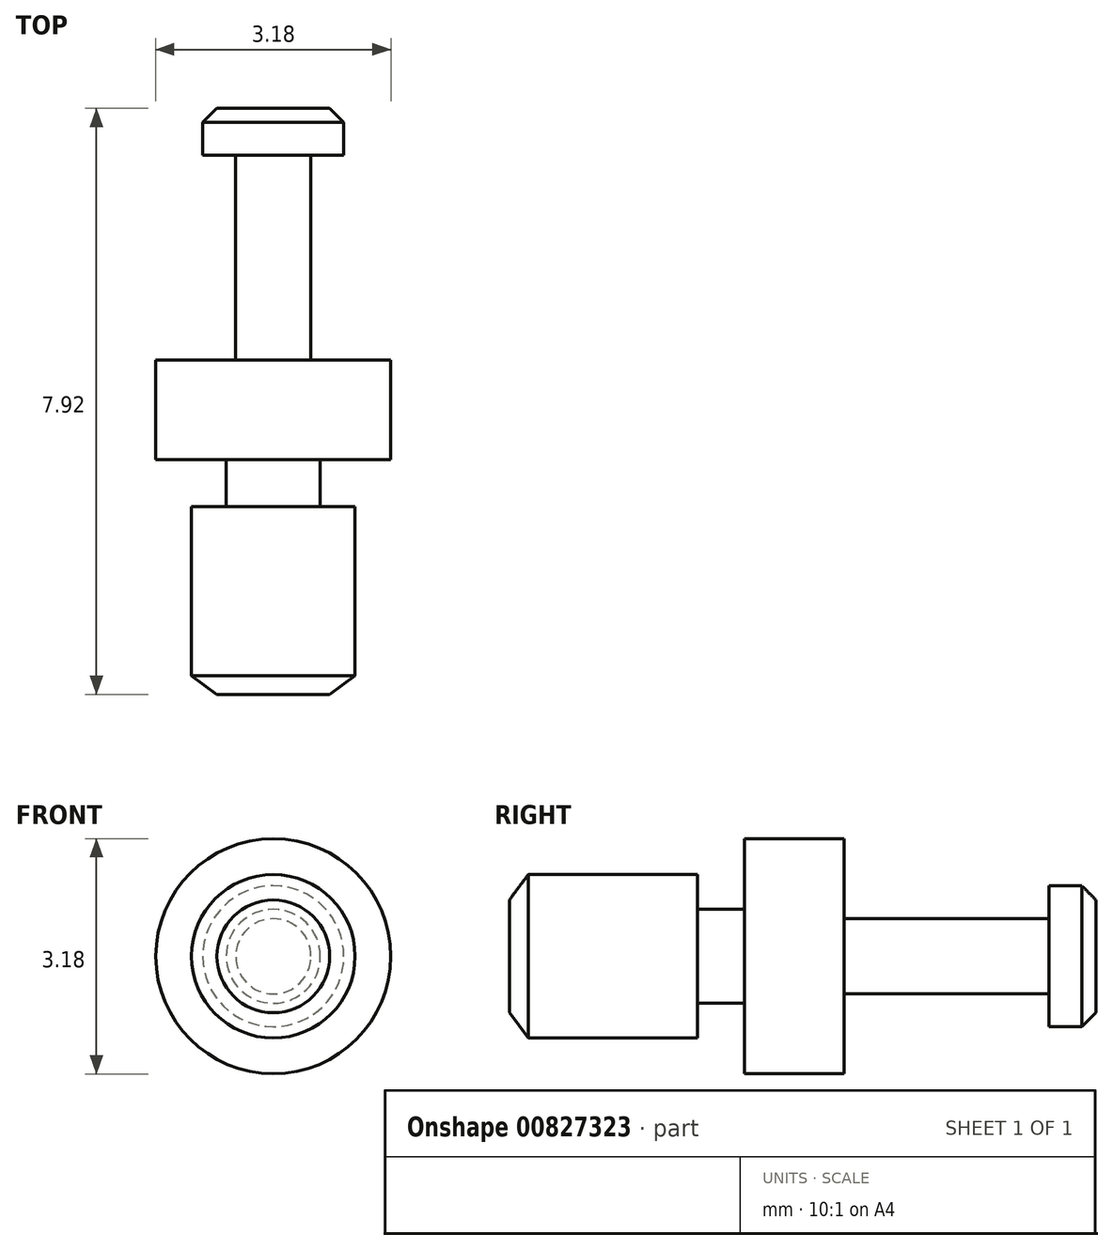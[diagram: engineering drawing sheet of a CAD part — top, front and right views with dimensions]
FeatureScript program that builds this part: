
annotation { "Feature Type Name" : "Feature", "Feature Type Description" : "" }
export const myFeature = defineFeature(function(context is Context, id is Id, definition is map)
    precondition{}
    {
        {
            var Q0;
            Q0=qCreatedBy(makeId("Top.planeOp"),FACE);
            var sketch = newSketch(context, id + "F0", { "sketchPlane" : qUnion([Q0])});
            skLineSegment(sketch, "E0", {"start": v(0, 7.92) * mm, "end": v(0, 0) * mm});
            skLineSegment(sketch, "E1", {"start": v(0, 7.92) * mm, "end": v(-0.76, 7.92) * mm});
            skLineSegment(sketch, "E2", {"start": v(-0.95, 7.29) * mm, "end": v(-0.5, 7.29) * mm});
            skLineSegment(sketch, "E3", {"start": v(-0.5, 7.29) * mm, "end": v(-0.5, 4.52) * mm});
            skLineSegment(sketch, "E4", {"start": v(-0.5, 4.52) * mm, "end": v(-1.59, 4.52) * mm});
            skLineSegment(sketch, "E5", {"start": v(-1.59, 4.52) * mm, "end": v(-1.59, 3.17) * mm});
            skLineSegment(sketch, "E6", {"start": v(-1.59, 3.17) * mm, "end": v(-0.63, 3.17) * mm});
            skLineSegment(sketch, "E7", {"start": v(-0.63, 3.17) * mm, "end": v(-0.63, 2.54) * mm});
            skLineSegment(sketch, "E8", {"start": v(-0.63, 2.54) * mm, "end": v(-1.1, 2.54) * mm});
            skLineSegment(sketch, "E9", {"start": v(0, 10.24) * mm, "end": v(0, -1.26) * mm, "construction": true});
            skLineSegment(sketch, "E10", {"start": v(-0.76, 7.92) * mm, "end": v(-0.95, 7.73) * mm});
            skLineSegment(sketch, "E11", {"start": v(-0.95, 7.73) * mm, "end": v(-0.95, 7.29) * mm});
            skLineSegment(sketch, "E12", {"start": v(-1.1, 2.54) * mm, "end": v(-1.1, 0.25) * mm});
            skLineSegment(sketch, "E13", {"start": v(-1.1, 0.25) * mm, "end": v(-0.76, 0) * mm});
            skLineSegment(sketch, "E14", {"start": v(-0.76, 0) * mm, "end": v(0, 0) * mm});
            skSolve(sketch);
        }
        {
            var Q0;
            Q0 = qSketchRegion(id + "F0", true);
            var Q1;
            Q1=sQuery(id+"F0.wireOp",EDGE,"E9");
            revolve(context, id + "F1", {"surfaceOperationType" : NewSurfaceOperationType.NEW, "entities" : qUnion([Q0]), "axis" : qUnion([Q1]), "revolveType" : RevolveType.FULL});
        }
    });
